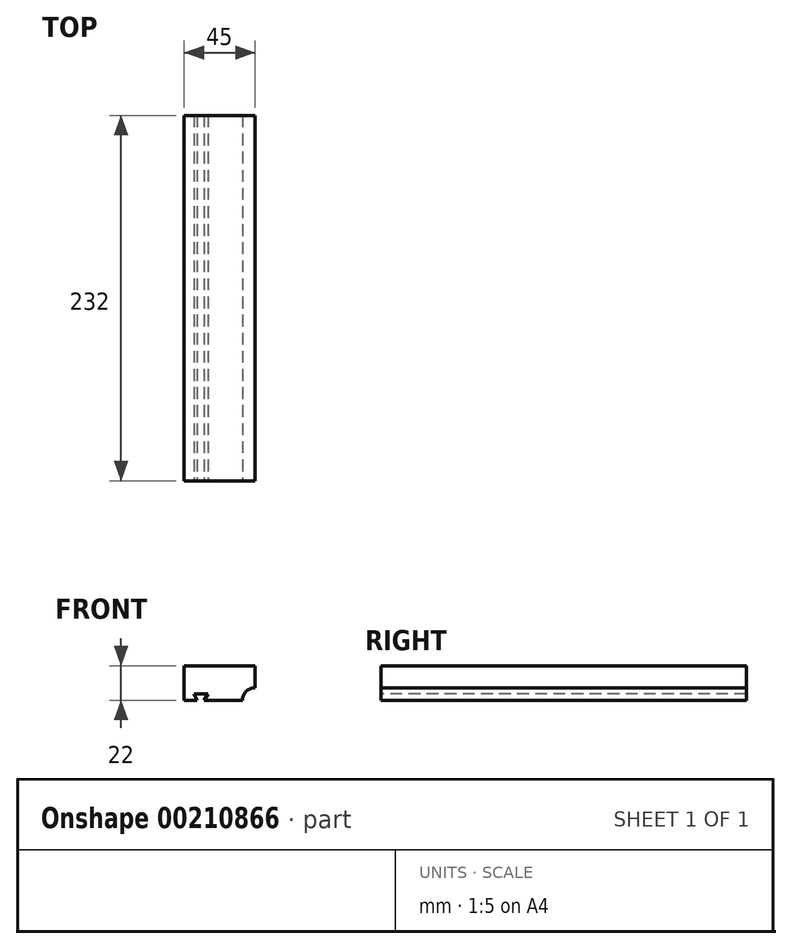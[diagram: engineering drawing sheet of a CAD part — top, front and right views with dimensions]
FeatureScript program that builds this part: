
annotation { "Feature Type Name" : "Feature", "Feature Type Description" : "" }
export const myFeature = defineFeature(function(context is Context, id is Id, definition is map)
    precondition{}
    {
        {
            var Q0;
            Q0=qCreatedBy(makeId("Front.planeOp"),FACE);
            var sketch = newSketch(context, id + "F0", { "sketchPlane" : qUnion([Q0])});
            skLineSegment(sketch, "E0.bottom", {"start": v(22.5, 11) * mm, "end": v(-22.5, 11) * mm});
            skLineSegment(sketch, "E0.top", {"start": v(14.5, -11) * mm, "end": v(-9.88, -11) * mm});
            skLineSegment(sketch, "E0.left", {"start": v(22.5, 11) * mm, "end": v(22.5, -3) * mm});
            skLineSegment(sketch, "E0.right", {"start": v(-22.5, 11) * mm, "end": v(-22.5, -11) * mm});
            skPoint(sketch, "E0.middle", {"position": v(0, 0) * mm});
            skArc(sketch, "E1", {"start": v(22.5, -3) * mm, "mid": v(16.84, -5.34) * mm, "end": v(14.5, -11) * mm});
            skLineSegment(sketch, "E2", {"start": v(-14.19, -11) * mm, "end": v(-16.27, -7.02) * mm});
            skLineSegment(sketch, "E3", {"start": v(-16.27, -7.02) * mm, "end": v(-7.33, -7.02) * mm});
            skLineSegment(sketch, "E4", {"start": v(-7.33, -7.02) * mm, "end": v(-9.88, -11) * mm});
            skLineSegment(sketch, "E5.trimOffspring", {"start": v(-14.19, -11) * mm, "end": v(-22.5, -11) * mm});
            skSolve(sketch);
        }
        {
            var Q0;
            Q0 = qSketchRegion(id + "F0", true);
            extrude(context, id + "F1", {"entities" : qUnion([Q0]), "oppositeDirection" : true, "depth" : 232 * mm});
        }
    });
